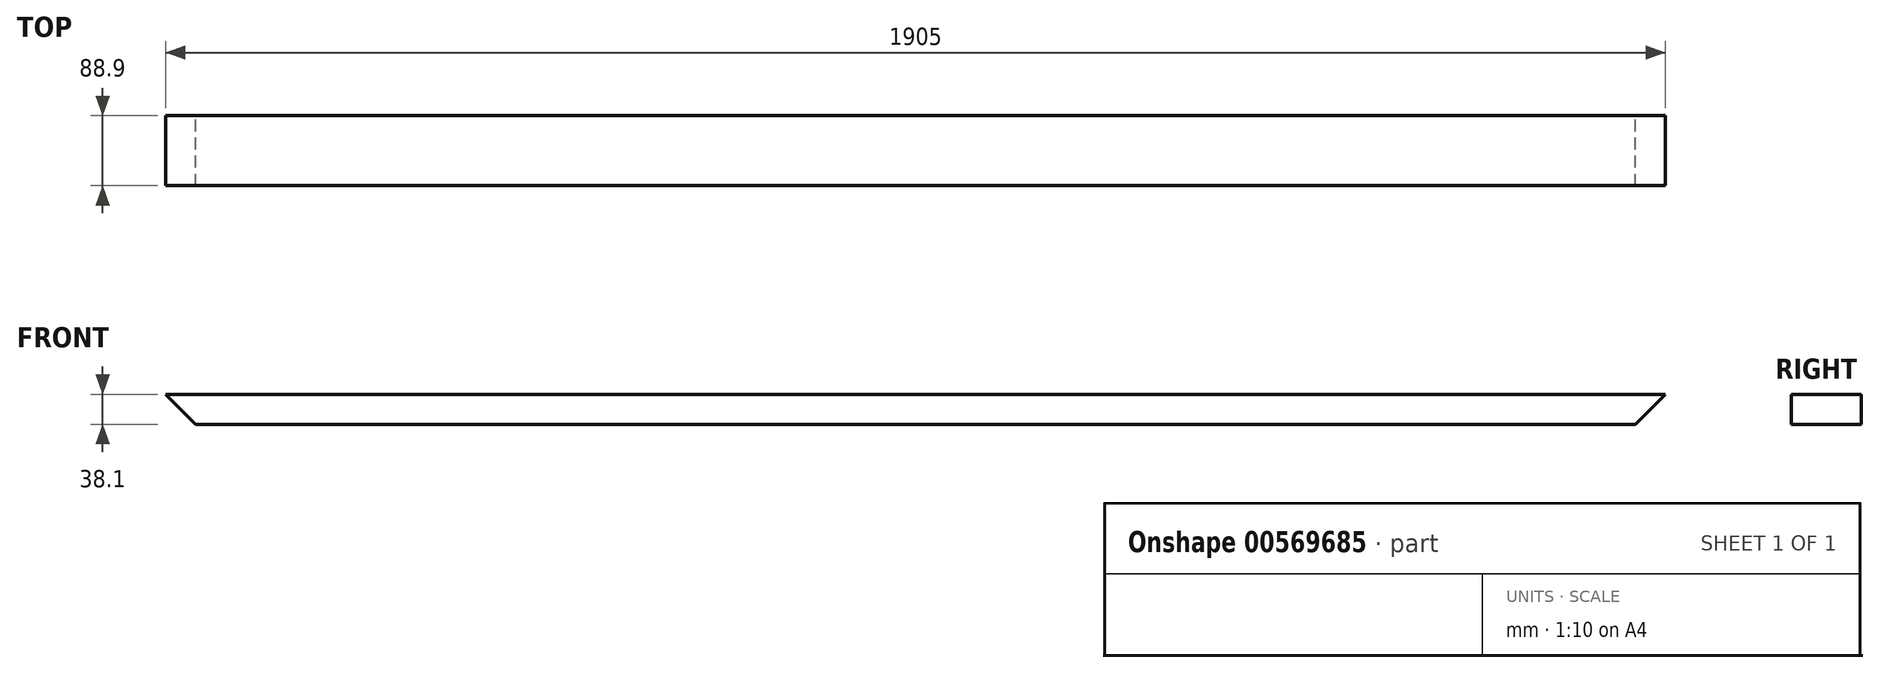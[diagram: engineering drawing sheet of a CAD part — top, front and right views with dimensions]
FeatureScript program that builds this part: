
annotation { "Feature Type Name" : "Feature", "Feature Type Description" : "" }
export const myFeature = defineFeature(function(context is Context, id is Id, definition is map)
    precondition{}
    {
        {
            var Q0;
            Q0=qCreatedBy(makeId("Front.planeOp"),FACE);
            var sketch = newSketch(context, id + "F0", { "sketchPlane" : qUnion([Q0])});
            skLineSegment(sketch, "E0", {"start": v(0, 0) * mm, "end": v(1905, 0) * mm});
            skLineSegment(sketch, "E1", {"start": v(1866.9, -38.1) * mm, "end": v(1905, 0) * mm});
            skLineSegment(sketch, "E2", {"start": v(1866.9, -38.1) * mm, "end": v(38.1, -38.1) * mm});
            skLineSegment(sketch, "E3", {"start": v(38.1, -38.1) * mm, "end": v(0, 0) * mm});
            skSolve(sketch);
        }
        {
            var Q0;
            Q0 = qSketchRegion(id + "F0", true);
            extrude(context, id + "F1", {"entities" : qUnion([Q0]), "depth" : 88.9 * mm, "offsetDistance" : 25.4 * mm});
        }
    });
